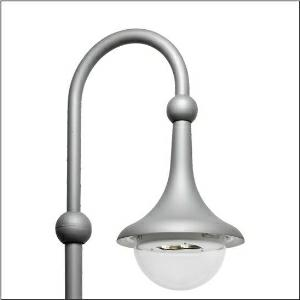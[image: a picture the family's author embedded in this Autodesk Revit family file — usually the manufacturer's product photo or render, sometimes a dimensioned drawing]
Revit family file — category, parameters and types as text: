
# Revit family: grosse_glocke_iq___st1_2a_5xa1565k1f108_5d30
name_source: partatom
category: Lighting Fixtures
units: mm (PartAtom-declared; Revit-internal decimal feet)

## family parameters
Cut with Voids When Loaded = No
Host = Face
Light Source = No
Part Type = Normal
Room Calculation Point = No
Round Connector Dimension = Use Diameter
Shared = No

## types (1)
- --- (1 x LED, 5420 lm, 34.3 W, 4000K)
    Apparent Load = 34 VA
    CIE Flux Codes = 28 66 95 100 100
    Color Rendering = 70
    Color Temperature = 4000K
    Default Elevation = 1800 mm
    Description = Large Bell iQ, mast luminaire, primary light control with 3 zone facetted reflector, of plastic, silver coated, primary optical cover: enclosure, of PMMA, transparent, light distribution: ST1.2a, light emission: direct distribution, primary light characteristic: asymmetric, installation type: suspended mounting, High Power LED, rated luminous flux: 5.420lm, luminous efficacy: 158lm/W, light colour: 740, colour temperature: 4000K, control gear: iQ Street-Remote, control: optimised constant luminous flux control (CLO 2.0), Desk-Remote (wireless, voltage-free reading and setting of iQ features in the workshop via application-optimized NFC function/RFID function), Light-Fading, Smart-Wire, Night-Set, Lumen-Switch, Temp-Guard, Auto-Match, Street-Remote, pre-setting: logarithmic dimming characteristic, mains connection: 230..240V, AC, 50/60Hz, start of lifetime: 34W, end of service life: 38W, reduction: 16W, luminaire housing, bell-shaped, of glass-fibre reinforced polyester, coated, Siteco® metallic grey (DB 702S), please order curved mast extension separately, diameter: 530mm, height: 695mm, mounting height: 4..6m, protection rating (complete): IP54, insulation class (complete): insulation class II (safety insulation), certification: CE, ENEC, VDE, impact resistance: IK08, standard-compliant lighting for roads and squares, packaging unit: 1 piece

Light Distribution: ST1.2a
    Height = 695 mm
    Lamp = 1 x LED
    Lamp Light Flux = 5420 lm
    Lamp Power = 34.3 W
    Lamp count = 1
    Length = 530 mm
    Luminous efficacy = 158 lm/W
    Manufacturer = Siteco
    ModVariant = No
    Model = 5XA1565K1F108
    Number of Poles = 1
    OnlyDefault = Yes
    Power Factor = 1
    Product Name = Große Glocke iQ | ST1.2a
    Product group = mast luminaire | pylon annexe
    ProductGroupID = 6200
    Protection Class = Protection class II
    Protection Degree = IP 54
    RLX_Detail_Level = 1
    RLX_Emergency_Light_Flux = 0 lm
    RLX_Emergency_Type = 0
    RLX_Emergency_Type_DB = No
    RlxData = <blob elided: 71777 chars, md5=0883b141>
    Socket = socket
    Standby Power = 0 W
    System Light Flux = 5420 lm
    System Power = 34 W
    Type Comments = factory setting: luminous flux: 100 % | dim-lin: 254 | 640 mA
    Type Image = l_1347688.jpg
    URL = http://relux.com
    VarID = @adj_079905
    Voltage = 0 V
    Weight = 0.00 kg
    Width = 0 mm  [stored 0 ft]

note: [stored X ft] marks values corroborated as IEEE doubles in the binary element streams (Revit-internal decimal feet)

## geometry (parser evidence)
native form markers: Blend x4, Sweep x10
no freeform markers — native parametric forms only
